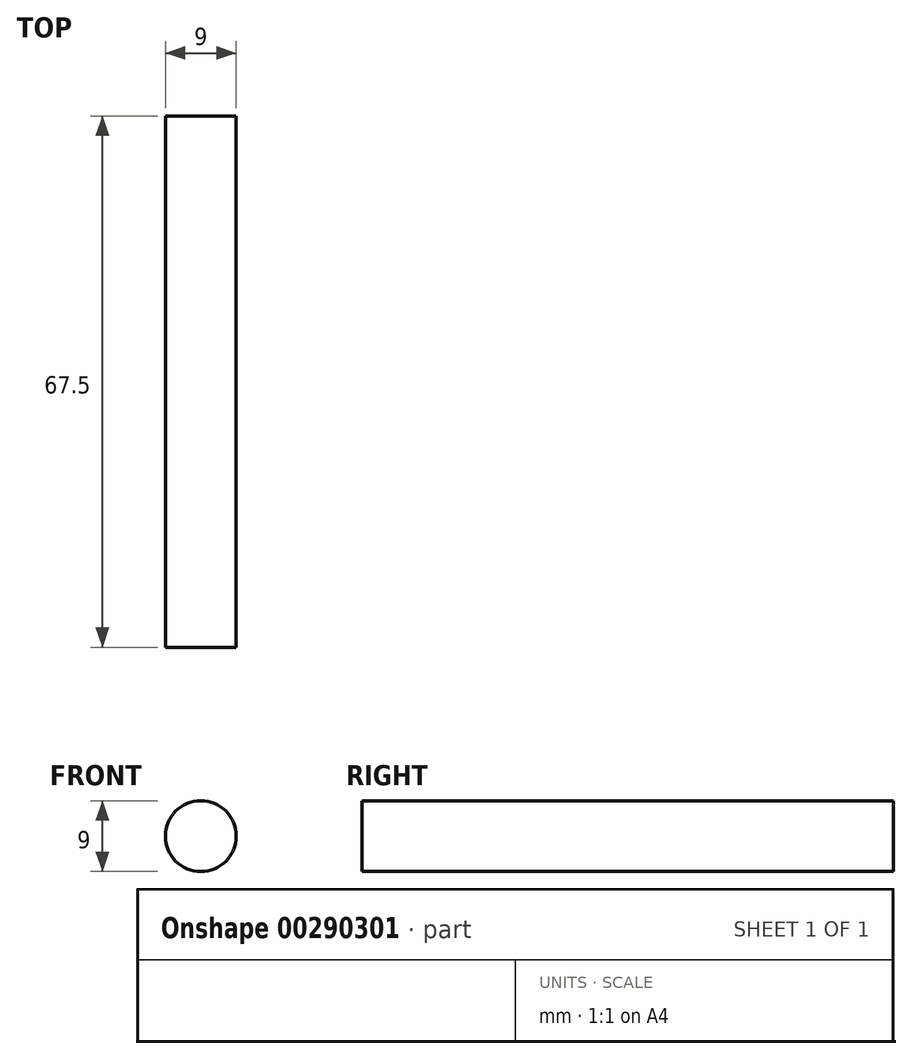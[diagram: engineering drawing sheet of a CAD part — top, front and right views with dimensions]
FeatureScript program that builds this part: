
annotation { "Feature Type Name" : "Feature", "Feature Type Description" : "" }
export const myFeature = defineFeature(function(context is Context, id is Id, definition is map)
    precondition{}
    {
        {
            var Q0;
            Q0=qCreatedBy(makeId("Front.planeOp"),FACE);
            var sketch = newSketch(context, id + "F0", { "sketchPlane" : qUnion([Q0])});
            skCircle(sketch, "E0", {"center": v(0, 0) * mm, "radius": 4.5 * mm});
            skSolve(sketch);
        }
        {
            var Q0;
            Q0=makeQuery(id+"F0.imprint","IMPRINT",FACE,{"disambiguationData":[TD([[makeQuery(id+"F0.imprint","IMPRINT",EDGE,{"derivedFrom":sQuery(id+"F0.wireOp",EDGE,"E0")}),1.0]])]});
            extrude(context, id + "F1", {"entities" : qUnion([Q0]), "endBound" : BoundingType.SYMMETRIC, "depth" : 45 * mm});
        }
        {
            var Q0;
            Q0=makeQuery(id+"F1.opExtrude","CAP_FACE",FACE,{"disambiguationData":[OSD([sQuery(id+"F0.wireOp",EDGE,"E0")])],"isStart":false});
            extrude(context, id + "F2", {"entities" : qUnion([Q0]), "operationType" : NewBodyOperationType.ADD, "endBound" : BoundingType.SYMMETRIC, "depth" : 45 * mm});
        }
    });
